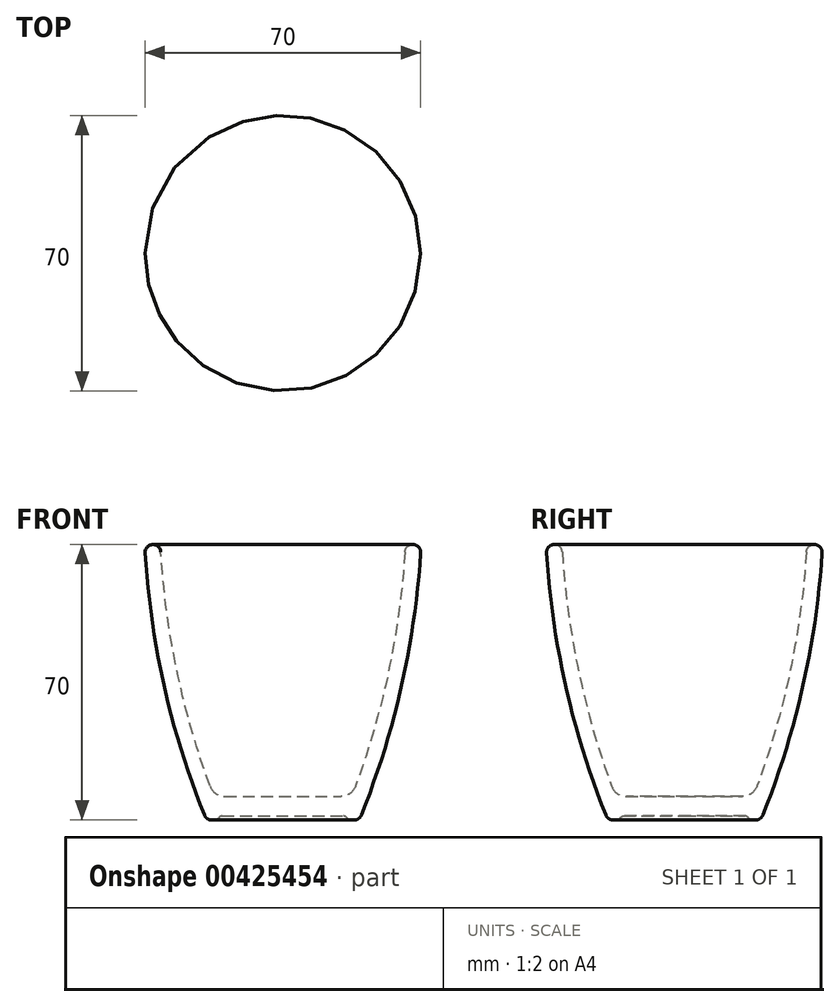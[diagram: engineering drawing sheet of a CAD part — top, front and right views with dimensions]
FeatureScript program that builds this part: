
annotation { "Feature Type Name" : "Feature", "Feature Type Description" : "" }
export const myFeature = defineFeature(function(context is Context, id is Id, definition is map)
    precondition{}
    {
        {
            var Q0;
            Q0=qCreatedBy(makeId("Front.planeOp"),FACE);
            var sketch = newSketch(context, id + "F0", { "sketchPlane" : qUnion([Q0])});
            skLineSegment(sketch, "E0", {"start": v(0, 1) * mm, "end": v(15.44, 1) * mm});
            skLineSegment(sketch, "E1", {"start": v(17.18, 0) * mm, "end": v(18.09, 0) * mm});
            skLineSegment(sketch, "E2", {"start": v(14.73, 6) * mm, "end": v(0, 6) * mm});
            skLineSegment(sketch, "E3", {"start": v(0, -14.42) * mm, "end": v(0, -11.95) * mm, "construction": true});
            skArc(sketch, "E4", {"start": v(35, 67.87) * mm, "mid": v(33.13, 70) * mm, "end": v(31, 68.13) * mm});
            skArc(sketch, "E5", {"start": v(19.94, 1.26) * mm, "mid": v(30.12, 33.97) * mm, "end": v(35, 67.87) * mm});
            skArc(sketch, "E6.0", {"start": v(18.49, 8.62) * mm, "mid": v(26.9, 37.92) * mm, "end": v(31, 68.13) * mm});
            skPoint(sketch, "E7.newPointB", {"position": v(31.04, 68.4) * mm});
            skLineSegment(sketch, "E7.filletArc", {"start": v(31, 68.13) * mm, "end": v(31, 68.13) * mm});
            skPoint(sketch, "E8.newPointA", {"position": v(16.7, 6) * mm});
            skArc(sketch, "E8.filletArc", {"start": v(14.73, 6) * mm, "mid": v(17.02, 6.72) * mm, "end": v(18.49, 8.62) * mm});
            skArc(sketch, "E9", {"start": v(15.44, 1) * mm, "mid": v(15.94, 0.87) * mm, "end": v(16.3, 0.5) * mm});
            skArc(sketch, "E10", {"start": v(17.18, 0) * mm, "mid": v(16.68, 0.13) * mm, "end": v(16.3, 0.5) * mm});
            skPoint(sketch, "E11.visualSharp", {"position": v(19.44, 0) * mm});
            skArc(sketch, "E11.filletArc", {"start": v(18.09, 0) * mm, "mid": v(19.2, 0.34) * mm, "end": v(19.94, 1.26) * mm});
            skLineSegment(sketch, "E12", {"start": v(0, 6) * mm, "end": v(0, 1) * mm});
            skLineSegment(sketch, "E13", {"start": v(0, 0) * mm, "end": v(0, 67.76) * mm});
            skLineSegment(sketch, "E14", {"start": v(0, 0) * mm, "end": v(-14.25, 0) * mm, "construction": true});
            skLineSegment(sketch, "E15.0.1.0", {"start": v(-0.02, 2) * mm, "end": v(-14.26, 2) * mm, "construction": true});
            skLineSegment(sketch, "E15.0.2.0", {"start": v(-0.04, 4) * mm, "end": v(-14.28, 4) * mm, "construction": true});
            skLineSegment(sketch, "E15.0.3.0", {"start": v(-0.06, 6) * mm, "end": v(-14.3, 6) * mm, "construction": true});
            skLineSegment(sketch, "E15.0.4.0", {"start": v(-0.07, 8) * mm, "end": v(-14.32, 8) * mm, "construction": true});
            skLineSegment(sketch, "E15.0.5.0", {"start": v(-0.1, 10) * mm, "end": v(-14.34, 10) * mm, "construction": true});
            skLineSegment(sketch, "E15.0.6.0", {"start": v(-0.11, 12) * mm, "end": v(-14.36, 12) * mm, "construction": true});
            skLineSegment(sketch, "E15.0.7.0", {"start": v(-0.13, 14) * mm, "end": v(-14.38, 14) * mm, "construction": true});
            skLineSegment(sketch, "E15.0.8.0", {"start": v(-0.15, 16) * mm, "end": v(-14.4, 16) * mm, "construction": true});
            skLineSegment(sketch, "E15.0.9.0", {"start": v(-0.17, 18) * mm, "end": v(-14.41, 18) * mm, "construction": true});
            skLineSegment(sketch, "E15.0.10.0", {"start": v(-0.19, 20) * mm, "end": v(-14.43, 20) * mm, "construction": true});
            skLineSegment(sketch, "E15.0.11.0", {"start": v(-0.2, 22) * mm, "end": v(-14.45, 22) * mm, "construction": true});
            skLineSegment(sketch, "E15.0.12.0", {"start": v(-0.22, 24) * mm, "end": v(-14.47, 24) * mm, "construction": true});
            skLineSegment(sketch, "E15.0.13.0", {"start": v(-0.24, 26) * mm, "end": v(-14.49, 26) * mm, "construction": true});
            skLineSegment(sketch, "E15.0.14.0", {"start": v(-0.26, 28) * mm, "end": v(-14.5, 28) * mm, "construction": true});
            skLineSegment(sketch, "E15.0.15.0", {"start": v(-0.28, 30) * mm, "end": v(-14.52, 30) * mm, "construction": true});
            skLineSegment(sketch, "E15.0.16.0", {"start": v(-0.3, 32) * mm, "end": v(-14.54, 32) * mm, "construction": true});
            skLineSegment(sketch, "E15.0.17.0", {"start": v(-0.32, 34) * mm, "end": v(-14.56, 34) * mm, "construction": true});
            skLineSegment(sketch, "E15.0.18.0", {"start": v(-0.33, 36) * mm, "end": v(-14.58, 36) * mm, "construction": true});
            skLineSegment(sketch, "E15.0.19.0", {"start": v(-0.35, 38) * mm, "end": v(-14.6, 38) * mm, "construction": true});
            skLineSegment(sketch, "E15.0.20.0", {"start": v(-0.37, 40) * mm, "end": v(-14.62, 40) * mm});
            skLineSegment(sketch, "E15.0.21.0", {"start": v(-0.4, 42) * mm, "end": v(-14.64, 42) * mm});
            skLineSegment(sketch, "E15.0.22.0", {"start": v(-0.4, 44) * mm, "end": v(-14.65, 44) * mm});
            skLineSegment(sketch, "E15.0.23.0", {"start": v(-0.43, 46) * mm, "end": v(-14.67, 46) * mm});
            skLineSegment(sketch, "E15.0.24.0", {"start": v(-0.45, 48) * mm, "end": v(-14.7, 48) * mm});
            skLineSegment(sketch, "E15.0.25.0", {"start": v(-0.46, 50) * mm, "end": v(-14.71, 50) * mm});
            skLineSegment(sketch, "E15.0.26.0", {"start": v(-0.48, 52) * mm, "end": v(-14.73, 52) * mm});
            skLineSegment(sketch, "E15.0.27.0", {"start": v(-0.5, 54) * mm, "end": v(-14.75, 54) * mm});
            skLineSegment(sketch, "E15.0.28.0", {"start": v(-0.52, 56) * mm, "end": v(-14.77, 56) * mm});
            skLineSegment(sketch, "E15.0.29.0", {"start": v(-0.54, 58) * mm, "end": v(-14.78, 58) * mm});
            skLineSegment(sketch, "E15.0.30.0", {"start": v(-0.56, 60) * mm, "end": v(-14.8, 60) * mm});
            skLineSegment(sketch, "E15.0.31.0", {"start": v(-0.58, 62) * mm, "end": v(-14.82, 62) * mm, "construction": true});
            skLineSegment(sketch, "E15.0.32.0", {"start": v(-0.6, 64) * mm, "end": v(-14.84, 64) * mm, "construction": true});
            skLineSegment(sketch, "E15.0.33.0", {"start": v(-0.61, 66) * mm, "end": v(-14.86, 66) * mm, "construction": true});
            skLineSegment(sketch, "E15.0.34.0", {"start": v(-0.63, 68) * mm, "end": v(-14.88, 68) * mm, "construction": true});
            skLineSegment(sketch, "E15.0.35.0", {"start": v(-0.65, 70) * mm, "end": v(-14.9, 70) * mm, "construction": true});
            skLineSegment(sketch, "E15.direction1", {"start": v(-14.25, 0) * mm, "end": v(41.35, -0.78) * mm, "construction": true});
            skLineSegment(sketch, "E15.direction2", {"start": v(-14.25, 0) * mm, "end": v(-14.26, 2) * mm, "construction": true});
            skLineSegment(sketch, "E16", {"start": v(-0.15, 16) * mm, "end": v(22.11, 16) * mm});
            skPoint(sketch, "E17", {"position": v(22.11, 16) * mm});
            skPoint(sketch, "E18", {"position": v(-0.15, 16) * mm});
            skPoint(sketch, "E19", {"position": v(-0.17, 18) * mm});
            skSolve(sketch);
        }
        {
            var Q0;
            Q0=makeQuery(id+"F0.imprint","IMPRINT",FACE,{"disambiguationData":[TD([[makeQuery(id+"F0.imprint","IMPRINT",EDGE,{"derivedFrom":sQuery(id+"F0.wireOp",EDGE,"E0")}),1.0]])]});
            var Q1;
            Q1=sQuery(id+"F0.wireOp",EDGE,"E13");
            revolve(context, id + "F1", {"surfaceOperationType" : NewSurfaceOperationType.NEW, "entities" : qUnion([Q0]), "axis" : qUnion([Q1]), "revolveType" : RevolveType.FULL});
        }
    });
